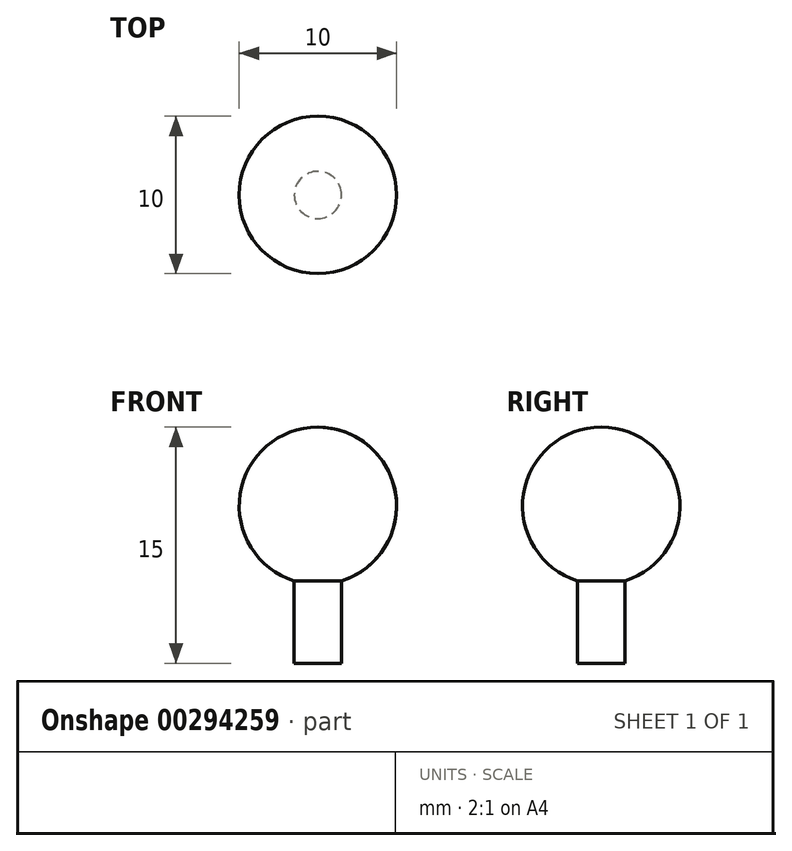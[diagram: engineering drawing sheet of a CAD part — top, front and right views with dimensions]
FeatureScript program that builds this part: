
annotation { "Feature Type Name" : "Feature", "Feature Type Description" : "" }
export const myFeature = defineFeature(function(context is Context, id is Id, definition is map)
    precondition{}
    {
        {
            var Q0;
            Q0=qCreatedBy(makeId("Front.planeOp"),FACE);
            var sketch = newSketch(context, id + "F0", { "sketchPlane" : qUnion([Q0])});
            skArc(sketch, "E0", {"start": v(1.5, -4.77) * mm, "mid": v(4.94, 0.76) * mm, "end": v(0, 5) * mm});
            skLineSegment(sketch, "E1.top", {"start": v(0, -10) * mm, "end": v(1.5, -10) * mm});
            skLineSegment(sketch, "E1.right", {"start": v(1.5, -4.77) * mm, "end": v(1.5, -10) * mm});
            skLineSegment(sketch, "E2", {"start": v(0, 5) * mm, "end": v(0, -10) * mm});
            skPoint(sketch, "E3.orphan", {"position": v(-1.5, 10) * mm});
            skPoint(sketch, "E4.orphan", {"position": v(1.5, 10) * mm});
            skPoint(sketch, "E5.orphan", {"position": v(-1.5, -10) * mm});
            skLineSegment(sketch, "E6", {"start": v(0, 11.13) * mm, "end": v(0, -23.05) * mm, "construction": true});
            skSolve(sketch);
        }
        {
            var Q0;
            Q0 = qSketchRegion(id + "F0", true);
            var Q1;
            Q1=sQuery(id+"F0.wireOp",EDGE,"E6");
            revolve(context, id + "F1", {"entities" : qUnion([Q0]), "axis" : qUnion([Q1]), "revolveType" : RevolveType.FULL});
        }
    });
